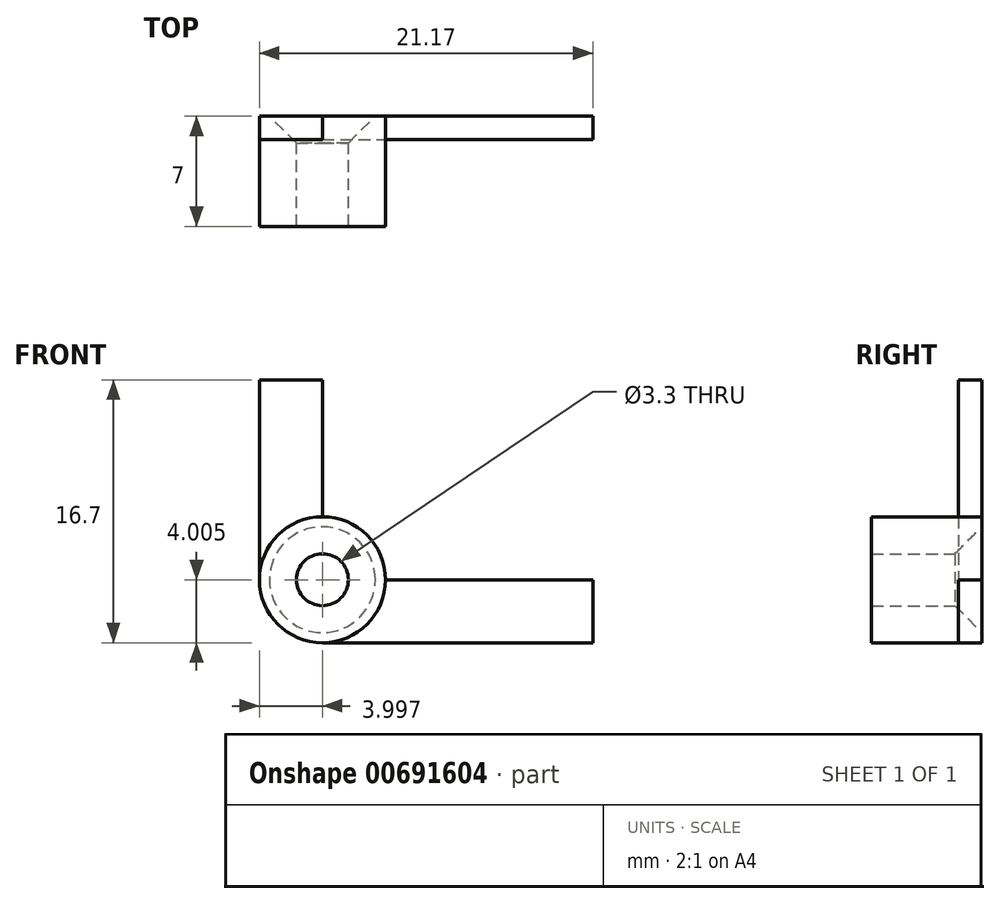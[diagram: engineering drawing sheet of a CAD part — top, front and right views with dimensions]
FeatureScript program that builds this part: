
annotation { "Feature Type Name" : "Feature", "Feature Type Description" : "" }
export const myFeature = defineFeature(function(context is Context, id is Id, definition is map)
    precondition{}
    {
        {
            var Q0;
            Q0=qCreatedBy(makeId("Front.planeOp"),FACE);
            var sketch = newSketch(context, id + "F0", { "sketchPlane" : qUnion([Q0])});
            skCircle(sketch, "E0", {"center": v(20.68, -27.05) * mm, "radius": 4 * mm});
            skLineSegment(sketch, "E1", {"start": v(20.68, -31.05) * mm, "end": v(37.85, -31.05) * mm});
            skLineSegment(sketch, "E2", {"start": v(37.85, -31.05) * mm, "end": v(37.85, -27.05) * mm});
            skLineSegment(sketch, "E3", {"start": v(37.85, -27.05) * mm, "end": v(24.68, -27.05) * mm});
            skLineSegment(sketch, "E4", {"start": v(16.68, -27.05) * mm, "end": v(16.68, -14.35) * mm});
            skLineSegment(sketch, "E5", {"start": v(16.68, -14.35) * mm, "end": v(20.68, -14.35) * mm});
            skLineSegment(sketch, "E6", {"start": v(20.68, -14.35) * mm, "end": v(20.68, -23.05) * mm});
            skSolve(sketch);
        }
        {
            var Q0;
            Q0=makeQuery(id+"F0.imprint","IMPRINT",FACE,{"disambiguationData":[TD([[makeQuery(id+"F0.imprint","IMPRINT",EDGE,{"derivedFrom":sQuery(id+"F0.wireOp",EDGE,"E0")}),1.0]])]});
            extrude(context, id + "F1", {"entities" : qUnion([Q0]), "depth" : 7 * mm, "offsetDistance" : 25 * mm});
        }
        {
            var Q0;
            Q0=qCreatedBy(makeId("Front.planeOp"),FACE);
            cPlane(context, id + "F2", {"entities" : qUnion([Q0]), "cplaneType" : CPlaneType.OFFSET, "offset" : 0.5 * mm, "width" : 150 * mm, "height" : 150 * mm});
        }
        {
            var Q0;
            Q0=sQuery(id+"F0.wireOp",VERTEX,"E0.center");
            var Q1;
            Q1=makeQuery(id+"F1.opExtrude","SWEPT_BODY",BODY,{"disambiguationData":[OSD([sQuery(id+"F0.wireOp",EDGE,"E0")])]});
            hole(context, id + "F3", {"style" : HoleStyle.C_SINK, "endStyle" : HoleEndStyle.THROUGH, "oppositeDirection" : true, "standardTappedOrClearance" : lookupTablePath({ "standard" : "ISO", "fit" : "Normal", "size" : "M3", "type" : "Clearance" }), "standardBlindInLast" : lookupTablePath({ "fit" : "Standard", "standard" : "ISO", "size" : "M3", "type" : "Clearance" }), "holeDiameter" : 3.3 * mm, "cSinkDiameter" : 6.72 * mm, "cSinkAngle" : 90 * degree, "majorDiameter" : 5 * mm, "isTappedThrough" : true, "tappedDepth" : 12 * mm, "tapClearance" : 3, "startFromSketch" : true, "locations" : qUnion([Q0]), "scope" : qUnion([Q1])});
        }
        {
            var Q0;
            {var subQ0=sQuery(id+"F0.wireOp",EDGE,"E4");Q0=makeQuery(id+"F0.imprint","IMPRINT",FACE,{"disambiguationData":[TD([[makeQuery(id+"F0.imprint","IMPRINT",EDGE,{"derivedFrom":subQ0}),-1.0]])]});}
            var Q1;
            {var subQ0=sQuery(id+"F0.wireOp",EDGE,"E1");Q1=makeQuery(id+"F0.imprint","IMPRINT",FACE,{"disambiguationData":[TD([[makeQuery(id+"F0.imprint","IMPRINT",EDGE,{"derivedFrom":subQ0}),1.0]])]});}
            extrude(context, id + "F4", {"entities" : qUnion([Q0, Q1]), "operationType" : NewBodyOperationType.ADD, "depth" : 1.5 * mm, "offsetDistance" : 25 * mm});
        }
    });
